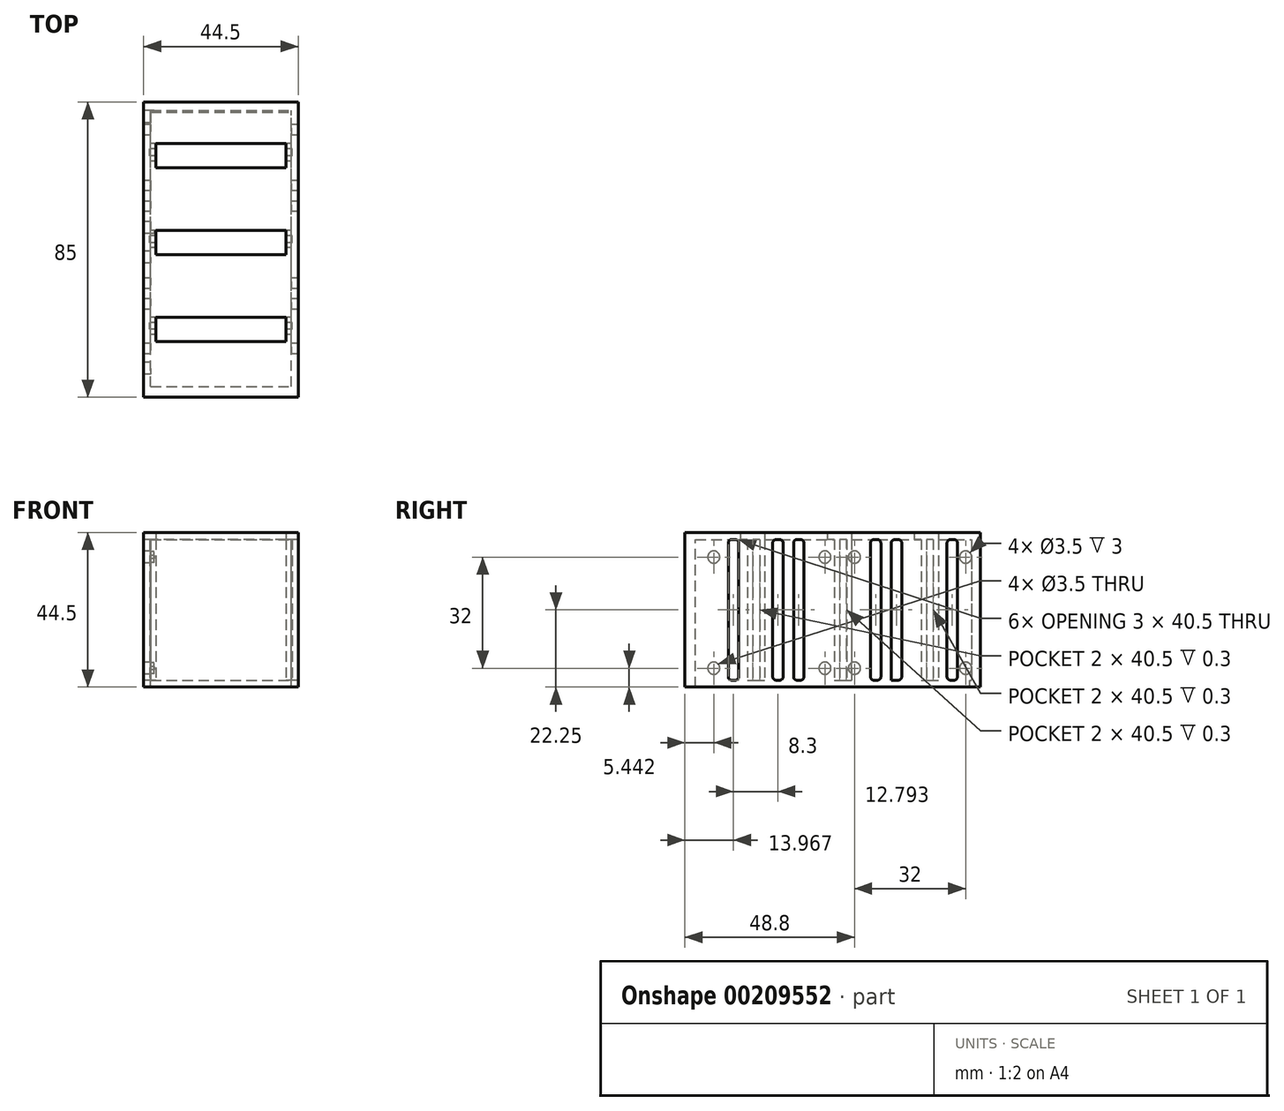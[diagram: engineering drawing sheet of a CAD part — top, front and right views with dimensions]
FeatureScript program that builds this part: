
annotation { "Feature Type Name" : "Feature", "Feature Type Description" : "" }
export const myFeature = defineFeature(function(context is Context, id is Id, definition is map)
    precondition{}
    {
        {
            var Q0;
            Q0=qCreatedBy(makeId("Front.planeOp"),FACE);
            var sketch = newSketch(context, id + "F0", { "sketchPlane" : qUnion([Q0])});
            skLineSegment(sketch, "E0.bottom", {"start": v(-20.25, 20.25) * mm, "end": v(20.25, 20.25) * mm});
            skLineSegment(sketch, "E0.top", {"start": v(-20.25, -20.25) * mm, "end": v(20.25, -20.25) * mm});
            skLineSegment(sketch, "E0.left", {"start": v(-20.25, 20.25) * mm, "end": v(-20.25, -20.25) * mm});
            skLineSegment(sketch, "E0.right", {"start": v(20.25, 20.25) * mm, "end": v(20.25, -20.25) * mm});
            skSolve(sketch);
        }
        {
            var Q0;
            Q0=qCreatedBy(makeId("Front.planeOp"),FACE);
            var sketch = newSketch(context, id + "F1", { "sketchPlane" : qUnion([Q0])});
            skLineSegment(sketch, "E1.bottom", {"start": v(-22.25, 22.25) * mm, "end": v(22.25, 22.25) * mm});
            skLineSegment(sketch, "E1.top", {"start": v(-22.25, -22.25) * mm, "end": v(22.25, -22.25) * mm});
            skLineSegment(sketch, "E1.left", {"start": v(-22.25, 22.25) * mm, "end": v(-22.25, -22.25) * mm});
            skLineSegment(sketch, "E1.right", {"start": v(22.25, 22.25) * mm, "end": v(22.25, -22.25) * mm});
            skSolve(sketch);
        }
        {
            var Q0;
            Q0=makeQuery(id+"F1.imprint","IMPRINT",FACE,{"disambiguationData":[TD([[makeQuery(id+"F1.imprint","IMPRINT",EDGE,{"derivedFrom":sQuery(id+"F1.wireOp",EDGE,"E1.bottom")}),-1.0]])]});
            extrude(context, id + "F2", {"entities" : qUnion([Q0]), "depth" : 85 * mm});
        }
        {
            var Q0;
            Q0=makeQuery(id+"F0.imprint","IMPRINT",FACE,{"disambiguationData":[TD([[makeQuery(id+"F0.imprint","IMPRINT",EDGE,{"derivedFrom":sQuery(id+"F0.wireOp",EDGE,"E0.bottom")}),-1.0]])]});
            extrude(context, id + "F3", {"entities" : qUnion([Q0]), "operationType" : NewBodyOperationType.REMOVE, "endBound" : BoundingType.UP_TO_NEXT, "depth" : 25 * mm});
        }
        {
            var Q0;
            Q0=qCreatedBy(makeId("Right.planeOp"),FACE);
            var sketch = newSketch(context, id + "F4", { "sketchPlane" : qUnion([Q0])});
            skLineSegment(sketch, "E2.bottom", {"start": v(-63.5, 20.25) * mm, "end": v(-62, 20.25) * mm});
            skLineSegment(sketch, "E2.top", {"start": v(-63.5, -20.25) * mm, "end": v(-62, -20.25) * mm});
            skLineSegment(sketch, "E2.left", {"start": v(-63.5, 20.25) * mm, "end": v(-63.5, -20.25) * mm});
            skLineSegment(sketch, "E2.right", {"start": v(-62, 20.25) * mm, "end": v(-62, -20.25) * mm});
            skLineSegment(sketch, "E3.bottom", {"start": v(-67, 20.25) * mm, "end": v(-65.5, 20.25) * mm});
            skLineSegment(sketch, "E3.top", {"start": v(-67, -20.25) * mm, "end": v(-65.5, -20.25) * mm});
            skLineSegment(sketch, "E3.left", {"start": v(-67, 20.25) * mm, "end": v(-67, -20.25) * mm});
            skLineSegment(sketch, "E3.right", {"start": v(-65.5, 20.25) * mm, "end": v(-65.5, -20.25) * mm});
            skLineSegment(sketch, "E4.bottom", {"start": v(-38.5, 20.25) * mm, "end": v(-37, 20.25) * mm});
            skLineSegment(sketch, "E4.top", {"start": v(-38.5, -20.25) * mm, "end": v(-37, -20.25) * mm});
            skLineSegment(sketch, "E4.left", {"start": v(-38.5, 20.25) * mm, "end": v(-38.5, -20.25) * mm});
            skLineSegment(sketch, "E4.right", {"start": v(-37, 20.25) * mm, "end": v(-37, -20.25) * mm});
            skLineSegment(sketch, "E5.bottom", {"start": v(-42, 20.25) * mm, "end": v(-40.5, 20.25) * mm});
            skLineSegment(sketch, "E5.top", {"start": v(-42, -20.25) * mm, "end": v(-40.5, -20.25) * mm});
            skLineSegment(sketch, "E5.left", {"start": v(-42, 20.25) * mm, "end": v(-42, -20.25) * mm});
            skLineSegment(sketch, "E5.right", {"start": v(-40.5, 20.25) * mm, "end": v(-40.5, -20.25) * mm});
            skLineSegment(sketch, "E6.bottom", {"start": v(-13.5, 20.25) * mm, "end": v(-12, 20.25) * mm});
            skLineSegment(sketch, "E6.top", {"start": v(-13.5, -20.25) * mm, "end": v(-12, -20.25) * mm});
            skLineSegment(sketch, "E6.left", {"start": v(-13.5, 20.25) * mm, "end": v(-13.5, -20.25) * mm});
            skLineSegment(sketch, "E6.right", {"start": v(-12, 20.25) * mm, "end": v(-12, -20.25) * mm});
            skLineSegment(sketch, "E7.bottom", {"start": v(-17, 20.25) * mm, "end": v(-15.5, 20.25) * mm});
            skLineSegment(sketch, "E7.top", {"start": v(-17, -20.25) * mm, "end": v(-15.5, -20.25) * mm});
            skLineSegment(sketch, "E7.left", {"start": v(-17, 20.25) * mm, "end": v(-17, -20.25) * mm});
            skLineSegment(sketch, "E7.right", {"start": v(-15.5, 20.25) * mm, "end": v(-15.5, -20.25) * mm});
            skSolve(sketch);
        }
        {
            var Q0;
            Q0=qCreatedBy(makeId("Top.planeOp"),FACE);
            var sketch = newSketch(context, id + "F5", { "sketchPlane" : qUnion([Q0])});
            skLineSegment(sketch, "E8.bottom", {"start": v(20.25, -82) * mm, "end": v(-20.25, -82) * mm});
            skLineSegment(sketch, "E8.top", {"start": v(-20.25, -3) * mm, "end": v(20.25, -3) * mm});
            skLineSegment(sketch, "E8.left", {"start": v(20.25, -82) * mm, "end": v(20.25, -3) * mm});
            skLineSegment(sketch, "E8.right", {"start": v(-20.25, -82) * mm, "end": v(-20.25, -3) * mm});
            skSolve(sketch);
        }
        {
            var Q0;
            Q0=makeQuery(id+"F5.imprint","IMPRINT",FACE,{"disambiguationData":[TD([[makeQuery(id+"F5.imprint","IMPRINT",EDGE,{"derivedFrom":sQuery(id+"F5.wireOp",EDGE,"E8.bottom")}),-1.0]])]});
            extrude(context, id + "F6", {"entities" : qUnion([Q0]), "operationType" : NewBodyOperationType.REMOVE, "endBound" : BoundingType.THROUGH_ALL, "oppositeDirection" : true, "depth" : 25 * mm});
        }
        {
            var Q0;
            Q0=makeQuery(id+"F4.imprint","IMPRINT",FACE,{"disambiguationData":[TD([[makeQuery(id+"F4.imprint","IMPRINT",EDGE,{"derivedFrom":sQuery(id+"F4.wireOp",EDGE,"E6.bottom")}),-1.0]])]});
            var Q1;
            Q1=makeQuery(id+"F4.imprint","IMPRINT",FACE,{"disambiguationData":[TD([[makeQuery(id+"F4.imprint","IMPRINT",EDGE,{"derivedFrom":sQuery(id+"F4.wireOp",EDGE,"E7.bottom")}),-1.0]])]});
            var Q2;
            Q2=makeQuery(id+"F4.imprint","IMPRINT",FACE,{"disambiguationData":[TD([[makeQuery(id+"F4.imprint","IMPRINT",EDGE,{"derivedFrom":sQuery(id+"F4.wireOp",EDGE,"E4.bottom")}),-1.0]])]});
            var Q3;
            Q3=makeQuery(id+"F4.imprint","IMPRINT",FACE,{"disambiguationData":[TD([[makeQuery(id+"F4.imprint","IMPRINT",EDGE,{"derivedFrom":sQuery(id+"F4.wireOp",EDGE,"E5.bottom")}),-1.0]])]});
            var Q4;
            Q4=makeQuery(id+"F4.imprint","IMPRINT",FACE,{"disambiguationData":[TD([[makeQuery(id+"F4.imprint","IMPRINT",EDGE,{"derivedFrom":sQuery(id+"F4.wireOp",EDGE,"E2.bottom")}),-1.0]])]});
            var Q5;
            Q5=makeQuery(id+"F4.imprint","IMPRINT",FACE,{"disambiguationData":[TD([[makeQuery(id+"F4.imprint","IMPRINT",EDGE,{"derivedFrom":sQuery(id+"F4.wireOp",EDGE,"E3.bottom")}),-1.0]])]});
            extrude(context, id + "F7", {"entities" : qUnion([Q0, Q1, Q2, Q3, Q4, Q5]), "operationType" : NewBodyOperationType.ADD, "endBound" : BoundingType.SYMMETRIC, "depth" : 40.5 * mm});
        }
        {
            var Q0;
            Q0=qCreatedBy(makeId("Front.planeOp"),FACE);
            var sketch = newSketch(context, id + "F8", { "sketchPlane" : qUnion([Q0])});
            skLineSegment(sketch, "E9.bottom", {"start": v(-18.75, 20.25) * mm, "end": v(18.75, 20.25) * mm});
            skLineSegment(sketch, "E9.top", {"start": v(-18.75, -20.25) * mm, "end": v(18.75, -20.25) * mm});
            skLineSegment(sketch, "E9.left", {"start": v(-18.75, 20.25) * mm, "end": v(-18.75, -20.25) * mm});
            skLineSegment(sketch, "E9.right", {"start": v(18.75, 20.25) * mm, "end": v(18.75, -20.25) * mm});
            skSolve(sketch);
        }
        {
            var Q0;
            Q0=makeQuery(id+"F8.imprint","IMPRINT",FACE,{"disambiguationData":[TD([[makeQuery(id+"F8.imprint","IMPRINT",EDGE,{"derivedFrom":sQuery(id+"F8.wireOp",EDGE,"E9.bottom")}),-1.0]])]});
            extrude(context, id + "F9", {"entities" : qUnion([Q0]), "operationType" : NewBodyOperationType.REMOVE, "endBound" : BoundingType.THROUGH_ALL, "depth" : 25 * mm});
        }
        {
            var Q0;
            Q0=qCreatedBy(makeId("Front.planeOp"),FACE);
            var sketch = newSketch(context, id + "F10", { "sketchPlane" : qUnion([Q0])});
            skLineSegment(sketch, "E10.bottom", {"start": v(-22.25, 22.25) * mm, "end": v(22.25, 22.25) * mm});
            skLineSegment(sketch, "E10.top", {"start": v(-22.25, -22.25) * mm, "end": v(22.25, -22.25) * mm});
            skLineSegment(sketch, "E10.left", {"start": v(-22.25, 22.25) * mm, "end": v(-22.25, -22.25) * mm});
            skLineSegment(sketch, "E10.right", {"start": v(22.25, 22.25) * mm, "end": v(22.25, -22.25) * mm});
            skSolve(sketch);
        }
        {
            var Q0;
            Q0 = qSketchRegion(id + "F10", true);
            extrude(context, id + "F11", {"entities" : qUnion([Q0]), "operationType" : NewBodyOperationType.ADD, "depth" : 2.5 * mm});
        }
        {
            var Q0;
            Q0=qCreatedBy(makeId("Top.planeOp"),FACE);
            var sketch = newSketch(context, id + "F12", { "sketchPlane" : qUnion([Q0])});
            skLineSegment(sketch, "E11.bottom", {"start": v(-18.75, -69) * mm, "end": v(18.75, -69) * mm});
            skLineSegment(sketch, "E11.top", {"start": v(-18.75, -62) * mm, "end": v(18.75, -62) * mm});
            skLineSegment(sketch, "E11.left", {"start": v(-18.75, -69) * mm, "end": v(-18.75, -62) * mm});
            skLineSegment(sketch, "E11.right", {"start": v(18.75, -69) * mm, "end": v(18.75, -62) * mm});
            skLineSegment(sketch, "E12.bottom", {"start": v(-18.75, -44) * mm, "end": v(18.75, -44) * mm});
            skLineSegment(sketch, "E12.top", {"start": v(-18.75, -37) * mm, "end": v(18.75, -37) * mm});
            skLineSegment(sketch, "E12.left", {"start": v(-18.75, -44) * mm, "end": v(-18.75, -37) * mm});
            skLineSegment(sketch, "E12.right", {"start": v(18.75, -44) * mm, "end": v(18.75, -37) * mm});
            skLineSegment(sketch, "E13.bottom", {"start": v(-18.75, -19) * mm, "end": v(18.75, -19) * mm});
            skLineSegment(sketch, "E13.top", {"start": v(-18.75, -12) * mm, "end": v(18.75, -12) * mm});
            skLineSegment(sketch, "E13.left", {"start": v(-18.75, -19) * mm, "end": v(-18.75, -12) * mm});
            skLineSegment(sketch, "E13.right", {"start": v(18.75, -19) * mm, "end": v(18.75, -12) * mm});
            skSolve(sketch);
        }
        {
            var Q0;
            Q0 = qSketchRegion(id + "F12", true);
            extrude(context, id + "F13", {"entities" : qUnion([Q0]), "operationType" : NewBodyOperationType.REMOVE, "depth" : 23.25 * mm});
        }
        {
            var Q0;
            Q0=makeQuery(id+"F2.opExtrude","CAP_FACE",FACE,{"disambiguationData":[OSD([sQuery(id+"F1.wireOp",EDGE,"E1.bottom"),sQuery(id+"F1.wireOp",EDGE,"E1.top"),sQuery(id+"F1.wireOp",EDGE,"E1.left"),sQuery(id+"F1.wireOp",EDGE,"E1.right")])],"isStart":false});
            var sketch = newSketch(context, id + "F14", { "sketchPlane" : qUnion([Q0])});
            skLineSegment(sketch, "E14.bottom", {"start": v(-20.25, 20.25) * mm, "end": v(20.25, 20.25) * mm});
            skLineSegment(sketch, "E14.top", {"start": v(-20.25, -20.25) * mm, "end": v(20.25, -20.25) * mm});
            skLineSegment(sketch, "E14.left", {"start": v(-20.25, 20.25) * mm, "end": v(-20.25, -20.25) * mm});
            skLineSegment(sketch, "E14.right", {"start": v(20.25, 20.25) * mm, "end": v(20.25, -20.25) * mm});
            skSolve(sketch);
        }
        {
            var Q0;
            Q0 = qSketchRegion(id + "F14", true);
            extrude(context, id + "F15", {"entities" : qUnion([Q0]), "operationType" : NewBodyOperationType.ADD, "oppositeDirection" : true, "depth" : 3 * mm});
        }
        {
            var Q0;
            Q0=makeQuery(id+"F2.opExtrude","SWEPT_FACE",FACE,{"disambiguationData":[OSD([sQuery(id+"F1.wireOp",EDGE,"E1.left")])]});
            var sketch = newSketch(context, id + "F16", { "sketchPlane" : qUnion([Q0])});
            skCircle(sketch, "E15", {"center": v(4.2, 15.2) * mm, "radius": 1.75 * mm});
            skCircle(sketch, "E16", {"center": v(4.2, -16.8) * mm, "radius": 1.75 * mm});
            skCircle(sketch, "E17", {"center": v(36.2, -16.8) * mm, "radius": 1.75 * mm});
            skCircle(sketch, "E18", {"center": v(36.2, 15.2) * mm, "radius": 1.75 * mm});
            skCircle(sketch, "E19", {"center": v(44.7, 15.2) * mm, "radius": 1.75 * mm});
            skCircle(sketch, "E20", {"center": v(44.7, -16.8) * mm, "radius": 1.75 * mm});
            skCircle(sketch, "E21", {"center": v(76.7, -16.8) * mm, "radius": 1.75 * mm});
            skCircle(sketch, "E22", {"center": v(76.7, 15.2) * mm, "radius": 1.75 * mm});
            skSolve(sketch);
        }
        {
            var Q0;
            Q0 = qSketchRegion(id + "F16", true);
            extrude(context, id + "F17", {"entities" : qUnion([Q0]), "operationType" : NewBodyOperationType.REMOVE, "oppositeDirection" : true, "depth" : 3 * mm});
        }
        {
            var Q0;
            Q0=makeQuery(id+"F2.opExtrude","SWEPT_FACE",FACE,{"disambiguationData":[OSD([sQuery(id+"F1.wireOp",EDGE,"E1.left")])]});
            var sketch = newSketch(context, id + "F18", { "sketchPlane" : qUnion([Q0])});
            skLineSegment(sketch, "E23.bottom", {"start": v(72.53, 20.25) * mm, "end": v(69.53, 20.25) * mm});
            skLineSegment(sketch, "E23.top", {"start": v(72.53, -20.25) * mm, "end": v(69.53, -20.25) * mm});
            skLineSegment(sketch, "E23.left", {"start": v(72.53, 20.25) * mm, "end": v(72.53, -20.25) * mm});
            skLineSegment(sketch, "E23.right", {"start": v(69.53, 20.25) * mm, "end": v(69.53, -20.25) * mm});
            skLineSegment(sketch, "E24.bottom", {"start": v(59.74, 20.25) * mm, "end": v(56.74, 20.25) * mm});
            skLineSegment(sketch, "E24.top", {"start": v(59.74, -20.25) * mm, "end": v(56.74, -20.25) * mm});
            skLineSegment(sketch, "E24.left", {"start": v(59.74, 20.25) * mm, "end": v(59.74, -20.25) * mm});
            skLineSegment(sketch, "E24.right", {"start": v(56.74, 20.25) * mm, "end": v(56.74, -20.25) * mm});
            skLineSegment(sketch, "E25.bottom", {"start": v(53.74, 20.25) * mm, "end": v(50.74, 20.25) * mm});
            skLineSegment(sketch, "E25.top", {"start": v(53.74, -20.25) * mm, "end": v(50.74, -20.25) * mm});
            skLineSegment(sketch, "E25.left", {"start": v(53.74, 20.25) * mm, "end": v(53.74, -20.25) * mm});
            skLineSegment(sketch, "E25.right", {"start": v(50.74, 20.25) * mm, "end": v(50.74, -20.25) * mm});
            skLineSegment(sketch, "E26.bottom", {"start": v(31.6, 20.25) * mm, "end": v(28.6, 20.25) * mm});
            skLineSegment(sketch, "E26.top", {"start": v(31.6, -20.25) * mm, "end": v(28.6, -20.25) * mm});
            skLineSegment(sketch, "E26.left", {"start": v(31.6, 20.25) * mm, "end": v(31.6, -20.25) * mm});
            skLineSegment(sketch, "E26.right", {"start": v(28.6, 20.25) * mm, "end": v(28.6, -20.25) * mm});
            skLineSegment(sketch, "E27.bottom", {"start": v(25.6, 20.25) * mm, "end": v(22.6, 20.25) * mm});
            skLineSegment(sketch, "E27.top", {"start": v(25.6, -20.25) * mm, "end": v(22.6, -20.25) * mm});
            skLineSegment(sketch, "E27.left", {"start": v(25.6, 20.25) * mm, "end": v(25.6, -20.25) * mm});
            skLineSegment(sketch, "E27.right", {"start": v(22.6, 20.25) * mm, "end": v(22.6, -20.25) * mm});
            skLineSegment(sketch, "E28.bottom", {"start": v(9.56, 20.25) * mm, "end": v(6.56, 20.25) * mm});
            skLineSegment(sketch, "E28.top", {"start": v(9.56, -20.25) * mm, "end": v(6.56, -20.25) * mm});
            skLineSegment(sketch, "E28.left", {"start": v(9.56, 20.25) * mm, "end": v(9.56, -20.25) * mm});
            skLineSegment(sketch, "E28.right", {"start": v(6.56, 20.25) * mm, "end": v(6.56, -20.25) * mm});
            skSolve(sketch);
        }
        {
            var Q0;
            Q0 = qSketchRegion(id + "F18", true);
            extrude(context, id + "F19", {"entities" : qUnion([Q0]), "operationType" : NewBodyOperationType.REMOVE, "oppositeDirection" : true, "depth" : 46.5 * mm});
        }
        {
            var Q0;
            Q0=makeQuery(id+"F19.boolean.opBoolean","COPY",EDGE,{"derivedFrom":makeQuery(id+"F19.opExtrude","SWEPT_EDGE",EDGE,{"disambiguationData":[OSD([sQuery(id+"F18.wireOp",EDGE,"E25.top"),sQuery(id+"F18.wireOp",EDGE,"E25.right")])]})});
            var Q1;
            Q1=makeQuery(id+"F19.boolean.opBoolean","COPY",EDGE,{"derivedFrom":makeQuery(id+"F19.opExtrude","SWEPT_EDGE",EDGE,{"disambiguationData":[OSD([sQuery(id+"F18.wireOp",EDGE,"E24.top"),sQuery(id+"F18.wireOp",EDGE,"E24.right")])]})});
            var Q2;
            Q2=makeQuery(id+"F19.boolean.opBoolean","COPY",EDGE,{"derivedFrom":makeQuery(id+"F19.opExtrude","SWEPT_EDGE",EDGE,{"disambiguationData":[OSD([sQuery(id+"F18.wireOp",EDGE,"E27.top"),sQuery(id+"F18.wireOp",EDGE,"E27.right")])]})});
            var Q3;
            Q3=makeQuery(id+"F19.boolean.opBoolean","COPY",EDGE,{"derivedFrom":makeQuery(id+"F19.opExtrude","SWEPT_EDGE",EDGE,{"disambiguationData":[OSD([sQuery(id+"F18.wireOp",EDGE,"E26.top"),sQuery(id+"F18.wireOp",EDGE,"E26.right")])]})});
            var Q4;
            Q4=makeQuery(id+"F19.boolean.opBoolean","COPY",EDGE,{"derivedFrom":makeQuery(id+"F19.opExtrude","SWEPT_EDGE",EDGE,{"disambiguationData":[OSD([sQuery(id+"F18.wireOp",EDGE,"E23.top"),sQuery(id+"F18.wireOp",EDGE,"E23.right")])]})});
            var Q5;
            Q5=makeQuery(id+"F19.boolean.opBoolean","COPY",EDGE,{"derivedFrom":makeQuery(id+"F19.opExtrude","SWEPT_EDGE",EDGE,{"disambiguationData":[OSD([sQuery(id+"F18.wireOp",EDGE,"E28.top"),sQuery(id+"F18.wireOp",EDGE,"E28.right")])]})});
            var Q6;
            Q6=makeQuery(id+"F19.boolean.opBoolean","COPY",EDGE,{"derivedFrom":makeQuery(id+"F19.opExtrude","SWEPT_EDGE",EDGE,{"disambiguationData":[OSD([sQuery(id+"F18.wireOp",EDGE,"E23.top"),sQuery(id+"F18.wireOp",EDGE,"E23.left")])]})});
            var Q7;
            Q7=makeQuery(id+"F19.boolean.opBoolean","COPY",EDGE,{"derivedFrom":makeQuery(id+"F19.opExtrude","SWEPT_EDGE",EDGE,{"disambiguationData":[OSD([sQuery(id+"F18.wireOp",EDGE,"E24.top"),sQuery(id+"F18.wireOp",EDGE,"E24.left")])]})});
            var Q8;
            Q8=makeQuery(id+"F19.boolean.opBoolean","COPY",EDGE,{"derivedFrom":makeQuery(id+"F19.opExtrude","SWEPT_EDGE",EDGE,{"disambiguationData":[OSD([sQuery(id+"F18.wireOp",EDGE,"E25.top"),sQuery(id+"F18.wireOp",EDGE,"E25.left")])]})});
            var Q9;
            Q9=makeQuery(id+"F19.boolean.opBoolean","COPY",EDGE,{"derivedFrom":makeQuery(id+"F19.opExtrude","SWEPT_EDGE",EDGE,{"disambiguationData":[OSD([sQuery(id+"F18.wireOp",EDGE,"E26.top"),sQuery(id+"F18.wireOp",EDGE,"E26.left")])]})});
            var Q10;
            Q10=makeQuery(id+"F19.boolean.opBoolean","COPY",EDGE,{"derivedFrom":makeQuery(id+"F19.opExtrude","SWEPT_EDGE",EDGE,{"disambiguationData":[OSD([sQuery(id+"F18.wireOp",EDGE,"E28.top"),sQuery(id+"F18.wireOp",EDGE,"E28.left")])]})});
            var Q11;
            Q11=makeQuery(id+"F19.boolean.opBoolean","COPY",EDGE,{"derivedFrom":makeQuery(id+"F19.opExtrude","SWEPT_EDGE",EDGE,{"disambiguationData":[OSD([sQuery(id+"F18.wireOp",EDGE,"E23.bottom"),sQuery(id+"F18.wireOp",EDGE,"E23.left")])]})});
            var Q12;
            Q12=makeQuery(id+"F19.boolean.opBoolean","COPY",EDGE,{"derivedFrom":makeQuery(id+"F19.opExtrude","SWEPT_EDGE",EDGE,{"disambiguationData":[OSD([sQuery(id+"F18.wireOp",EDGE,"E23.bottom"),sQuery(id+"F18.wireOp",EDGE,"E23.right")])]})});
            var Q13;
            Q13=makeQuery(id+"F19.boolean.opBoolean","COPY",EDGE,{"derivedFrom":makeQuery(id+"F19.opExtrude","SWEPT_EDGE",EDGE,{"disambiguationData":[OSD([sQuery(id+"F18.wireOp",EDGE,"E24.bottom"),sQuery(id+"F18.wireOp",EDGE,"E24.right")])]})});
            var Q14;
            Q14=makeQuery(id+"F19.boolean.opBoolean","COPY",EDGE,{"derivedFrom":makeQuery(id+"F19.opExtrude","SWEPT_EDGE",EDGE,{"disambiguationData":[OSD([sQuery(id+"F18.wireOp",EDGE,"E25.bottom"),sQuery(id+"F18.wireOp",EDGE,"E25.right")])]})});
            var Q15;
            Q15=makeQuery(id+"F19.boolean.opBoolean","COPY",EDGE,{"derivedFrom":makeQuery(id+"F19.opExtrude","SWEPT_EDGE",EDGE,{"disambiguationData":[OSD([sQuery(id+"F18.wireOp",EDGE,"E26.bottom"),sQuery(id+"F18.wireOp",EDGE,"E26.right")])]})});
            var Q16;
            Q16=makeQuery(id+"F19.boolean.opBoolean","COPY",EDGE,{"derivedFrom":makeQuery(id+"F19.opExtrude","SWEPT_EDGE",EDGE,{"disambiguationData":[OSD([sQuery(id+"F18.wireOp",EDGE,"E27.bottom"),sQuery(id+"F18.wireOp",EDGE,"E27.right")])]})});
            var Q17;
            Q17=makeQuery(id+"F19.boolean.opBoolean","COPY",EDGE,{"derivedFrom":makeQuery(id+"F19.opExtrude","SWEPT_EDGE",EDGE,{"disambiguationData":[OSD([sQuery(id+"F18.wireOp",EDGE,"E28.bottom"),sQuery(id+"F18.wireOp",EDGE,"E28.right")])]})});
            var Q18;
            Q18=makeQuery(id+"F19.boolean.opBoolean","COPY",EDGE,{"derivedFrom":makeQuery(id+"F19.opExtrude","SWEPT_EDGE",EDGE,{"disambiguationData":[OSD([sQuery(id+"F18.wireOp",EDGE,"E24.bottom"),sQuery(id+"F18.wireOp",EDGE,"E24.left")])]})});
            var Q19;
            Q19=makeQuery(id+"F19.boolean.opBoolean","COPY",EDGE,{"derivedFrom":makeQuery(id+"F19.opExtrude","SWEPT_EDGE",EDGE,{"disambiguationData":[OSD([sQuery(id+"F18.wireOp",EDGE,"E25.bottom"),sQuery(id+"F18.wireOp",EDGE,"E25.left")])]})});
            var Q20;
            Q20=makeQuery(id+"F19.boolean.opBoolean","COPY",EDGE,{"derivedFrom":makeQuery(id+"F19.opExtrude","SWEPT_EDGE",EDGE,{"disambiguationData":[OSD([sQuery(id+"F18.wireOp",EDGE,"E26.bottom"),sQuery(id+"F18.wireOp",EDGE,"E26.left")])]})});
            var Q21;
            Q21=makeQuery(id+"F19.boolean.opBoolean","COPY",EDGE,{"derivedFrom":makeQuery(id+"F19.opExtrude","SWEPT_EDGE",EDGE,{"disambiguationData":[OSD([sQuery(id+"F18.wireOp",EDGE,"E27.bottom"),sQuery(id+"F18.wireOp",EDGE,"E27.left")])]})});
            var Q22;
            Q22=makeQuery(id+"F19.boolean.opBoolean","COPY",EDGE,{"derivedFrom":makeQuery(id+"F19.opExtrude","SWEPT_EDGE",EDGE,{"disambiguationData":[OSD([sQuery(id+"F18.wireOp",EDGE,"E28.bottom"),sQuery(id+"F18.wireOp",EDGE,"E28.left")])]})});
            fillet(context, id + "F20", {"entities" : qUnion([Q0, Q1, Q2, Q3, Q4, Q5, Q6, Q7, Q8, Q9, Q10, Q11, Q12, Q13, Q14, Q15, Q16, Q17, Q18, Q19, Q20, Q21, Q22]), "radius" : 1 * mm, "tangentPropagation" : true, "allowEdgeOverflow" : false});
        }
        {
            var Q0;
            Q0=makeQuery(id+"F6.boolean.opBoolean","MERGE",FACE,{"derivedFrom":[makeQuery(id+"F3.boolean.opBoolean","COPY",FACE,{"derivedFrom":makeQuery(id+"F3.opExtrude","SWEPT_FACE",FACE,{"disambiguationData":[OSD([sQuery(id+"F0.wireOp",EDGE,"E0.left")])]})}),makeQuery(id+"F6.opExtrude","SWEPT_FACE",FACE,{"disambiguationData":[OSD([sQuery(id+"F5.wireOp",EDGE,"E8.right")])]})]});
            var sketch = newSketch(context, id + "F21", { "sketchPlane" : qUnion([Q0])});
            skLineSegment(sketch, "E29", {"start": v(-65.5, -20.25) * mm, "end": v(-63.5, -20.25) * mm});
            skLineSegment(sketch, "E30", {"start": v(-63.5, -20.25) * mm, "end": v(-63.5, 20.25) * mm});
            skLineSegment(sketch, "E31", {"start": v(-63.5, 20.25) * mm, "end": v(-65.5, 20.25) * mm});
            skLineSegment(sketch, "E32", {"start": v(-65.5, 20.25) * mm, "end": v(-65.5, -20.25) * mm});
            skSolve(sketch);
        }
        {
            var Q0;
            Q0=makeQuery(id+"F21.imprint","IMPRINT",FACE,{"disambiguationData":[TD([[makeQuery(id+"F21.imprint","IMPRINT",EDGE,{"derivedFrom":sQuery(id+"F21.wireOp",EDGE,"E29")}),1.0]])]});
            extrude(context, id + "F22", {"entities" : qUnion([Q0]), "operationType" : NewBodyOperationType.REMOVE, "oppositeDirection" : true, "depth" : 0.3 * mm});
        }
        {
            var Q0;
            Q0=makeQuery(id+"F6.boolean.opBoolean","MERGE",FACE,{"derivedFrom":[makeQuery(id+"F3.boolean.opBoolean","COPY",FACE,{"derivedFrom":makeQuery(id+"F3.opExtrude","SWEPT_FACE",FACE,{"disambiguationData":[OSD([sQuery(id+"F0.wireOp",EDGE,"E0.left")])]})}),makeQuery(id+"F6.opExtrude","SWEPT_FACE",FACE,{"disambiguationData":[OSD([sQuery(id+"F5.wireOp",EDGE,"E8.right")])]})]});
            var sketch = newSketch(context, id + "F23", { "sketchPlane" : qUnion([Q0])});
            skLineSegment(sketch, "E33", {"start": v(-38.5, 20.25) * mm, "end": v(-40.5, 20.25) * mm});
            skLineSegment(sketch, "E34", {"start": v(-40.5, 20.25) * mm, "end": v(-40.5, -20.25) * mm});
            skLineSegment(sketch, "E35", {"start": v(-40.5, -20.25) * mm, "end": v(-38.5, -20.25) * mm});
            skLineSegment(sketch, "E36", {"start": v(-38.5, -20.25) * mm, "end": v(-38.5, 20.25) * mm});
            skLineSegment(sketch, "E37", {"start": v(-13.5, 20.25) * mm, "end": v(-15.5, 20.25) * mm});
            skLineSegment(sketch, "E38", {"start": v(-15.5, 20.25) * mm, "end": v(-15.5, -20.25) * mm});
            skLineSegment(sketch, "E39", {"start": v(-15.5, -20.25) * mm, "end": v(-13.5, -20.25) * mm});
            skLineSegment(sketch, "E40", {"start": v(-13.5, -20.25) * mm, "end": v(-13.5, 20.25) * mm});
            skSolve(sketch);
        }
        {
            var Q0;
            Q0 = qSketchRegion(id + "F23", true);
            extrude(context, id + "F24", {"entities" : qUnion([Q0]), "operationType" : NewBodyOperationType.REMOVE, "oppositeDirection" : true, "depth" : 0.3 * mm});
        }
        {
            var Q0;
            Q0=makeQuery(id+"F6.boolean.opBoolean","MERGE",FACE,{"derivedFrom":[makeQuery(id+"F3.boolean.opBoolean","COPY",FACE,{"derivedFrom":makeQuery(id+"F3.opExtrude","SWEPT_FACE",FACE,{"disambiguationData":[OSD([sQuery(id+"F0.wireOp",EDGE,"E0.right")])]})}),makeQuery(id+"F6.opExtrude","SWEPT_FACE",FACE,{"disambiguationData":[OSD([sQuery(id+"F5.wireOp",EDGE,"E8.left")])]})]});
            var sketch = newSketch(context, id + "F25", { "sketchPlane" : qUnion([Q0])});
            skLineSegment(sketch, "E41", {"start": v(65.5, -20.25) * mm, "end": v(63.5, -20.25) * mm});
            skLineSegment(sketch, "E42", {"start": v(63.5, -20.25) * mm, "end": v(63.5, 20.25) * mm});
            skLineSegment(sketch, "E43", {"start": v(63.5, 20.25) * mm, "end": v(65.5, 20.25) * mm});
            skLineSegment(sketch, "E44", {"start": v(65.5, 20.25) * mm, "end": v(65.5, -20.25) * mm});
            skLineSegment(sketch, "E45", {"start": v(40.5, -20.25) * mm, "end": v(38.5, -20.25) * mm});
            skLineSegment(sketch, "E46", {"start": v(38.5, -20.25) * mm, "end": v(38.5, 20.25) * mm});
            skLineSegment(sketch, "E47", {"start": v(38.5, 20.25) * mm, "end": v(40.5, 20.25) * mm});
            skLineSegment(sketch, "E48", {"start": v(40.5, 20.25) * mm, "end": v(40.5, -20.25) * mm});
            skLineSegment(sketch, "E49", {"start": v(15.5, -20.25) * mm, "end": v(13.5, -20.25) * mm});
            skLineSegment(sketch, "E50", {"start": v(13.5, -20.25) * mm, "end": v(13.5, 20.25) * mm});
            skLineSegment(sketch, "E51", {"start": v(13.5, 20.25) * mm, "end": v(15.5, 20.25) * mm});
            skLineSegment(sketch, "E52", {"start": v(15.5, 20.25) * mm, "end": v(15.5, -20.25) * mm});
            skSolve(sketch);
        }
        {
            var Q0;
            Q0 = qSketchRegion(id + "F25", true);
            extrude(context, id + "F26", {"entities" : qUnion([Q0]), "operationType" : NewBodyOperationType.REMOVE, "oppositeDirection" : true, "depth" : 0.3 * mm});
        }
    });
